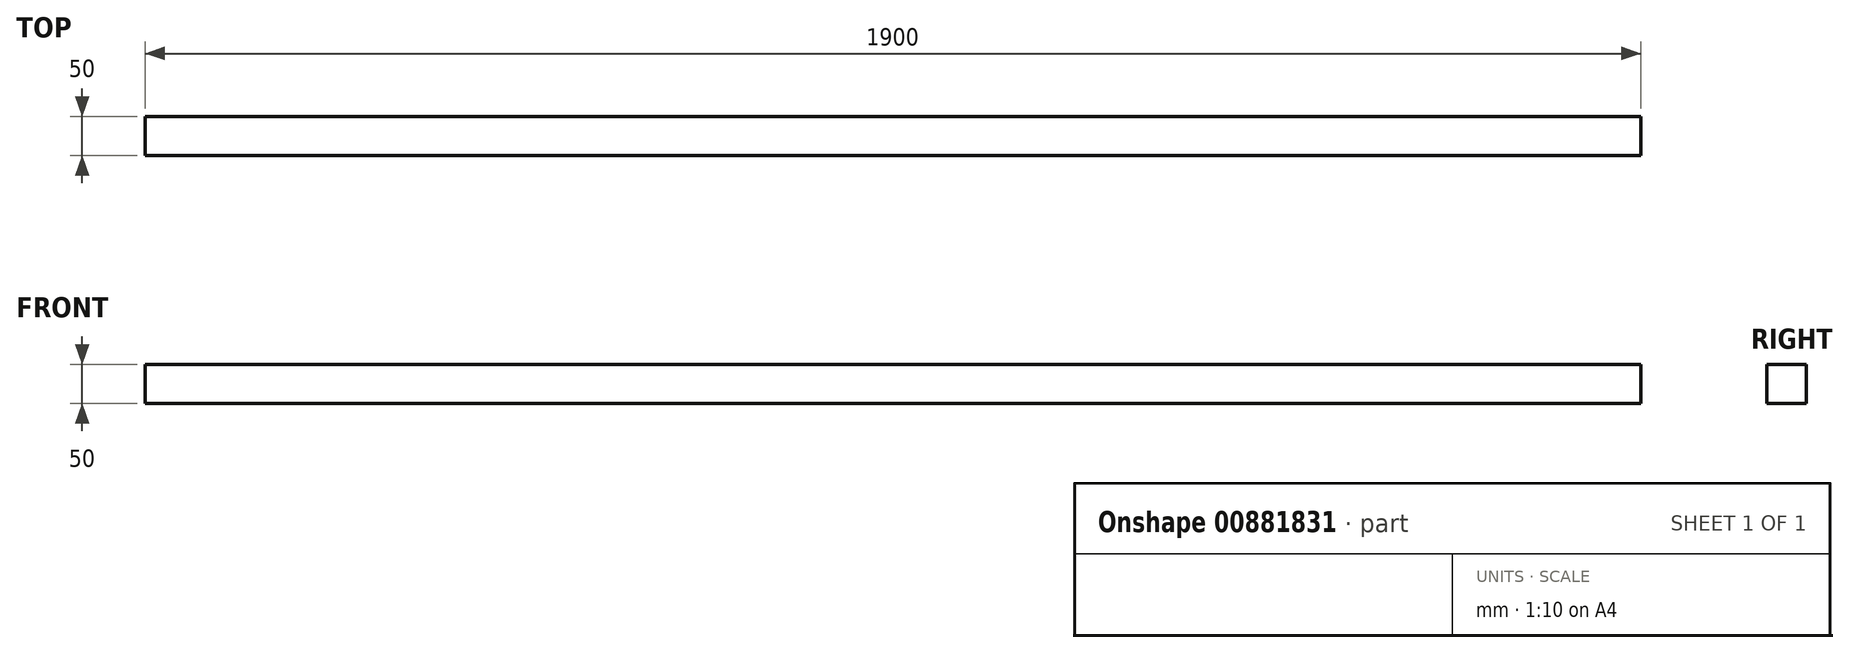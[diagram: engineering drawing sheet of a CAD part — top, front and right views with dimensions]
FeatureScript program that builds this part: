
annotation { "Feature Type Name" : "Feature", "Feature Type Description" : "" }
export const myFeature = defineFeature(function(context is Context, id is Id, definition is map)
    precondition{}
    {
        {
            var Q0;
            Q0=qCreatedBy(makeId("Front.planeOp"),FACE);
            var sketch = newSketch(context, id + "F0", { "sketchPlane" : qUnion([Q0])});
            skLineSegment(sketch, "E0", {"start": v(-48.8, 25.89) * mm, "end": v(1851.2, 25.89) * mm});
            skLineSegment(sketch, "E1", {"start": v(1851.2, 75.89) * mm, "end": v(-48.8, 75.89) * mm});
            skLineSegment(sketch, "E2", {"start": v(-48.8, 75.89) * mm, "end": v(-48.8, 25.89) * mm});
            skLineSegment(sketch, "E3", {"start": v(1851.2, 25.89) * mm, "end": v(1851.2, 75.89) * mm});
            skSolve(sketch);
        }
        {
            var Q0;
            Q0=qSketchRegion(id+"F0",true);
            extrude(context, id + "F1", {"entities" : qUnion([Q0]), "depth" : 50 * mm, "offsetDistance" : 25 * mm});
        }
    });
